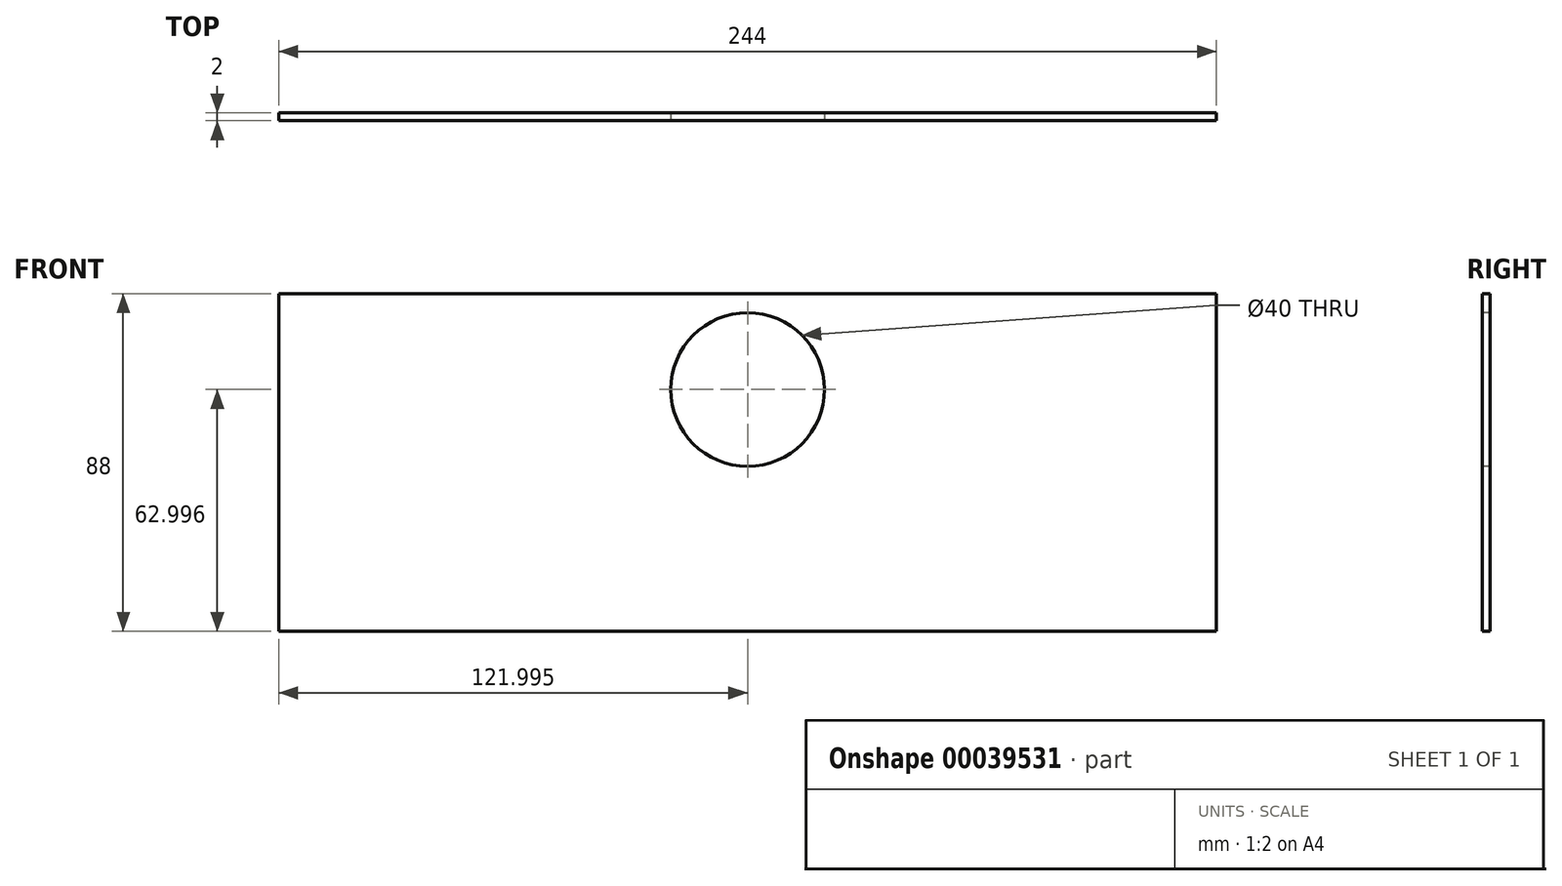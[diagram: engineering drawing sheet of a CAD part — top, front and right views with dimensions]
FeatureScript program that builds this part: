
annotation { "Feature Type Name" : "Feature", "Feature Type Description" : "" }
export const myFeature = defineFeature(function(context is Context, id is Id, definition is map)
    precondition{}
    {
        {
            var Q0;
            Q0=qCreatedBy(makeId("Front.planeOp"),FACE);
            var sketch = newSketch(context, id + "F0", { "sketchPlane" : qUnion([Q0])});
            skLineSegment(sketch, "E0.bottom", {"start": v(-84.4, 33.33) * mm, "end": v(159.6, 33.33) * mm});
            skLineSegment(sketch, "E0.top", {"start": v(-84.4, -54.67) * mm, "end": v(159.6, -54.67) * mm});
            skLineSegment(sketch, "E0.left", {"start": v(-84.4, 33.33) * mm, "end": v(-84.4, -54.67) * mm});
            skLineSegment(sketch, "E0.right", {"start": v(159.6, 33.33) * mm, "end": v(159.6, -54.67) * mm});
            skCircle(sketch, "E1", {"center": v(37.6, 8.33) * mm, "radius": 20 * mm});
            skSolve(sketch);
        }
        {
            var Q0;
            Q0=makeQuery(id+"F0.imprint","IMPRINT",FACE,{"disambiguationData":[TD([[makeQuery(id+"F0.imprint","IMPRINT",EDGE,{"derivedFrom":sQuery(id+"F0.wireOp",EDGE,"E0.bottom")}),-1.0]])]});
            extrude(context, id + "F1", {"entities" : qUnion([Q0]), "oppositeDirection" : true, "depth" : 2 * mm});
        }
    });
